# Revit family: Sink-Vessel-Lavatory-KOHLER-CHORD-K-2331T
name_source: partatom
category: Plumbing Fixtures
revit_build: Autodesk Revit 2017 (Build: 20160225_1515(x64)
units: mm (PartAtom-declared; Revit-internal decimal feet)

## family parameters
Cut with Voids When Loaded = No
Host = Face
OmniClass Number = 23.31.13.00
OmniClass Title = Sinks
Part Type = Normal
Room Calculation Point = No
Round Connector Dimension = Use Diameter
Shared = No

## types (6) — shared parameters
ADA Compliant = No
Assembly Code = D2010400
CW Connection = No
Cold Water Inlet = Cold Water Inlet
Date Modified = 05/29/2020
Default Elevation = 36"
Drain Included = No
HW Connection = No
Height = 5 3/4"
Hot Water Inlet = Hot Water Inlet
Length = 16 13/16"
Manufacturer = KOHLER Co.
MasterFormat 1995 = 15410
MasterFormat 2004 = 22.41.16
Material = Vitreous China
Product Name = CHORD
URL = http://www.kohler.com.cn
Vent Connection = No
Waste Connection = Yes
Waste Water Outlet = Waste Water Outlet
WaterSense Certified = No
Width = 18 5/8"

## per-type parameters (varying)
| type | 2331_8 | Description | Finish | Model | Type |
| Single faucet hole, 0-White | No | CHORD VESSEL LAVATORY, Single HOLE | Kohler-Vitreous_China-0-White | K-2331T-1-0 | 1 |
| 8" widespread faucet holes, 0-White | Yes | Lavatory 8 inch hole | Kohler-Vitreous_China-0-White | K-2331T-8-0 | 4 |
| Single faucet hole,47-Almond | No | CHORD VESSEL LAVATORY, Single HOLE | Kohler-Vitreous_China-47-Almond | K-2331T-1-47 | 2 |
| Single faucet hole,96-Biscuit | No | CHORD VESSEL LAVATORY, Single HOLE | Kohler-Vitreous_China-96-Biscuit | K-2331T-1-96 | 3 |
| 8" widespread faucet holes,47-Almond | Yes | Lavatory 8 inch hole | Kohler-Vitreous_China-47-Almond | K-2331T-8-47 | 5 |
| 8" widespread faucet holes,96-Biscuit | Yes | Lavatory 8 inch hole | Kohler-Vitreous_China-96-Biscuit | K-2331T-8-96 | 6 |

## geometry (parser evidence)
native form markers: Sweep x6
no freeform markers — native parametric forms only
